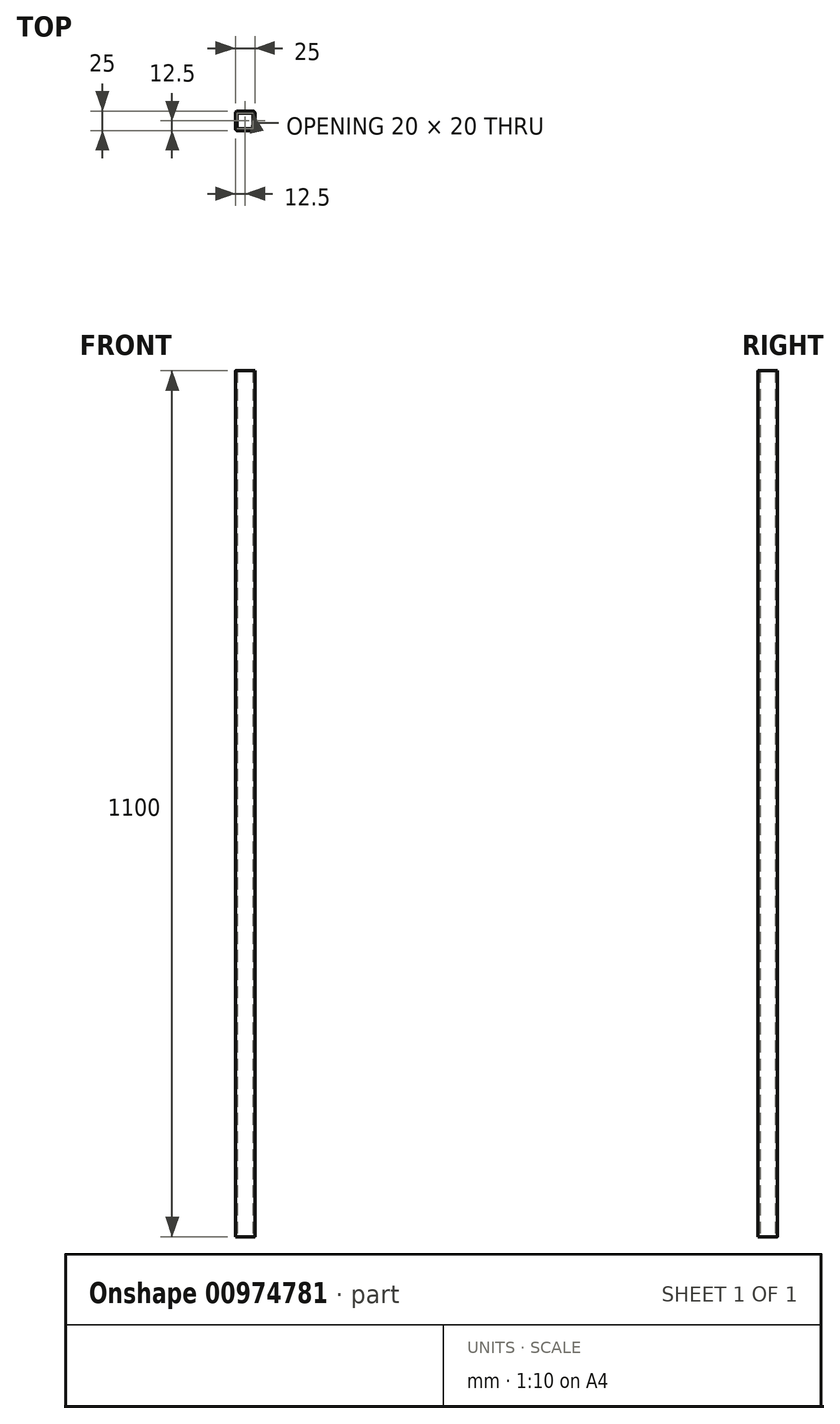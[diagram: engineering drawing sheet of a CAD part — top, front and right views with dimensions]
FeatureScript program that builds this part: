
annotation { "Feature Type Name" : "Feature", "Feature Type Description" : "" }
export const myFeature = defineFeature(function(context is Context, id is Id, definition is map)
    precondition{}
    {
        {
            var Q0;
            Q0=qCreatedBy(makeId("Top.planeOp"),FACE);
            var sketch = newSketch(context, id + "F0", { "sketchPlane" : qUnion([Q0])});
            skLineSegment(sketch, "E0.bottom", {"start": v(12.5, 12.5) * mm, "end": v(-12.5, 12.5) * mm});
            skLineSegment(sketch, "E0.top", {"start": v(12.5, -12.5) * mm, "end": v(-12.5, -12.5) * mm});
            skLineSegment(sketch, "E0.left", {"start": v(12.5, 12.5) * mm, "end": v(12.5, -12.5) * mm});
            skLineSegment(sketch, "E0.right", {"start": v(-12.5, 12.5) * mm, "end": v(-12.5, -12.5) * mm});
            skPoint(sketch, "E0.middle", {"position": v(0, 0) * mm});
            skLineSegment(sketch, "E1.bottom", {"start": v(10, 10) * mm, "end": v(-10, 10) * mm});
            skLineSegment(sketch, "E1.top", {"start": v(10, -10) * mm, "end": v(-10, -10) * mm});
            skLineSegment(sketch, "E1.left", {"start": v(10, 10) * mm, "end": v(10, -10) * mm});
            skLineSegment(sketch, "E1.right", {"start": v(-10, 10) * mm, "end": v(-10, -10) * mm});
            skSolve(sketch);
        }
        {
            var Q0;
            Q0 = qSketchRegion(id + "F0", true);
            extrude(context, id + "F1", {"entities" : qUnion([Q0]), "depth" : 1100 * mm, "offsetDistance" : 25 * mm});
        }
        {
            var Q0;
            Q0=makeQuery(id+"F1.opExtrude","SWEPT_EDGE",EDGE,{"disambiguationData":[OSD([sQuery(id+"F0.wireOp",EDGE,"E1.bottom"),sQuery(id+"F0.wireOp",EDGE,"E1.right")])]});
            var Q1;
            Q1=makeQuery(id+"F1.opExtrude","SWEPT_EDGE",EDGE,{"disambiguationData":[OSD([sQuery(id+"F0.wireOp",EDGE,"E1.bottom"),sQuery(id+"F0.wireOp",EDGE,"E1.left")])]});
            var Q2;
            Q2=makeQuery(id+"F1.opExtrude","SWEPT_EDGE",EDGE,{"disambiguationData":[OSD([sQuery(id+"F0.wireOp",EDGE,"E1.top"),sQuery(id+"F0.wireOp",EDGE,"E1.left")])]});
            var Q3;
            Q3=makeQuery(id+"F1.opExtrude","SWEPT_EDGE",EDGE,{"disambiguationData":[OSD([sQuery(id+"F0.wireOp",EDGE,"E1.top"),sQuery(id+"F0.wireOp",EDGE,"E1.right")])]});
            fillet(context, id + "F2", {"entities" : qUnion([Q0, Q1, Q2, Q3]), "radius" : 0.5 * mm, "tangentPropagation" : true, "allowEdgeOverflow" : false});
        }
        {
            var Q0;
            Q0=makeQuery(id+"F1.opExtrude","SWEPT_EDGE",EDGE,{"disambiguationData":[OSD([sQuery(id+"F0.wireOp",EDGE,"E0.bottom"),sQuery(id+"F0.wireOp",EDGE,"E0.left")])]});
            var Q1;
            Q1=makeQuery(id+"F1.opExtrude","SWEPT_EDGE",EDGE,{"disambiguationData":[OSD([sQuery(id+"F0.wireOp",EDGE,"E0.bottom"),sQuery(id+"F0.wireOp",EDGE,"E0.right")])]});
            var Q2;
            Q2=makeQuery(id+"F1.opExtrude","SWEPT_EDGE",EDGE,{"disambiguationData":[OSD([sQuery(id+"F0.wireOp",EDGE,"E0.top"),sQuery(id+"F0.wireOp",EDGE,"E0.left")])]});
            var Q3;
            Q3=makeQuery(id+"F1.opExtrude","SWEPT_EDGE",EDGE,{"disambiguationData":[OSD([sQuery(id+"F0.wireOp",EDGE,"E0.top"),sQuery(id+"F0.wireOp",EDGE,"E0.right")])]});
            fillet(context, id + "F3", {"entities" : qUnion([Q0, Q1, Q2, Q3]), "radius" : 3 * mm, "tangentPropagation" : true, "allowEdgeOverflow" : false});
        }
    });
